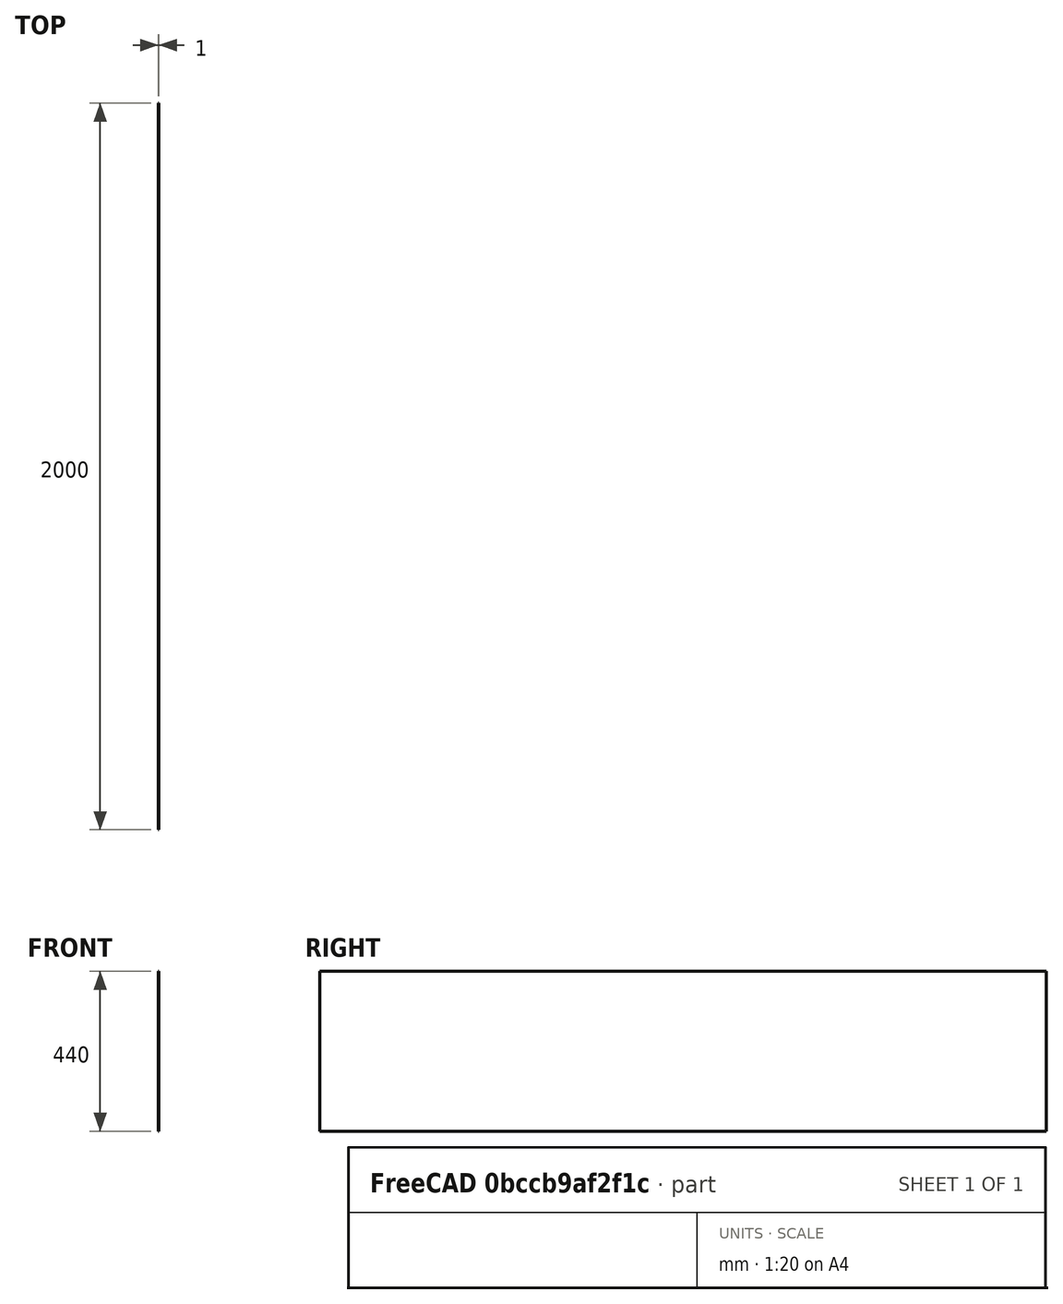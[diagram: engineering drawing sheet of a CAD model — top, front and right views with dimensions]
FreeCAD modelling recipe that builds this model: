
FCSTD DOCUMENT  (FreeCAD 1.0R38641 +468 (Git))
Label: chca-plech
License: All rights reserved
LicenseURL: https://en.wikipedia.org/wiki/All_rights_reserved
objects: Sketcher::SketchObject×1, PartDesign::Pad×1, PartDesign::Body×1
note: 6 computed .brp shape members not serialized (recipe doc carries the construction recipe); baked Part::Feature solids carry a one-line shape summary decoded from their .brp

FEATURE [Sketcher::SketchObject] Sketch
  ArcFitTolerance = 1e-06
  AttachmentSupport = -> [XZ_Plane]
  FullyConstrained = true
  MakeInternals = false
  MapMode = 5
  Placement = pos=(0,0,0) rot=(1,0,0;1.5708rad)
  sketch-geometry (4):
    g0: LineSegment StartX=0 StartY=0 StartZ=0 EndX=1 EndY=0 EndZ=0
    g1: LineSegment StartX=1 StartY=0 StartZ=0 EndX=1 EndY=440 EndZ=0
    g2: LineSegment StartX=1 StartY=440 StartZ=0 EndX=0 EndY=440 EndZ=0
    g3: LineSegment StartX=0 StartY=440 StartZ=0 EndX=0 EndY=0 EndZ=0
  constraints (11):
    c: Coincident(g0,g1)
    c: Coincident(g1,g2)
    c: Coincident(g2,g3)
    c: Coincident(g3,g0)
    c: Horizontal(g0)
    c: Horizontal(g2)
    c: Vertical(g1)
    c: Vertical(g3)
    c: Coincident(g0,g-1)
    c: DistanceY(g1,g1) = 440
    c: DistanceX(g0,g0) = 1
FEATURE [PartDesign::Pad] Pad
  Direction = (0,-1,2e-16)
  Length = 2000
  Length2 = 10
  Placement = pos=(0,0,0) rot=(1,0,0;1.5708rad)
  Profile = -> Sketch
  ReferenceAxis = -> Sketch [N_Axis]
  Refine = true
  Suppressed = false
  Type = 0
FEATURE [PartDesign::Body] Body  label="chca-plech"
  AllowCompound = false
  Group = -> [Sketch,Pad]
  Origin = -> Origin
  Tip = -> Pad
